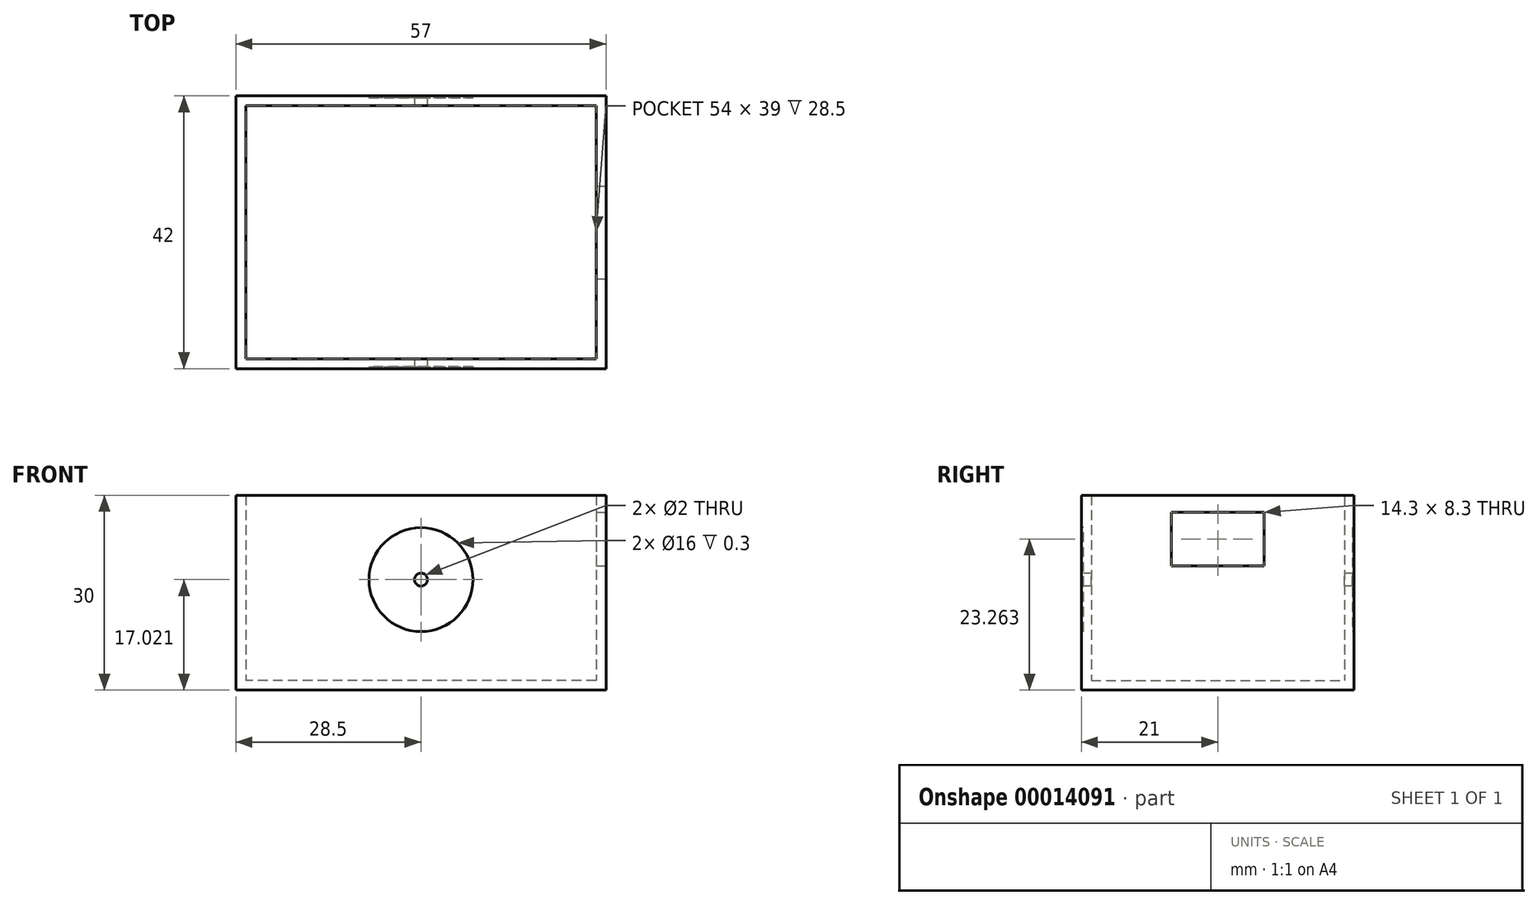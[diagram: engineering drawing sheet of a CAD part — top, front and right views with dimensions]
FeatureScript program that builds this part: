
annotation { "Feature Type Name" : "Feature", "Feature Type Description" : "" }
export const myFeature = defineFeature(function(context is Context, id is Id, definition is map)
    precondition{}
    {
        {
            var Q0;
            Q0=qCreatedBy(makeId("Top.planeOp"),FACE);
            var sketch = newSketch(context, id + "F0", { "sketchPlane" : qUnion([Q0])});
            skLineSegment(sketch, "E0.rect.bottom", {"start": v(28.5, -21) * mm, "end": v(-28.5, -21) * mm});
            skLineSegment(sketch, "E0.rect.top", {"start": v(28.5, 21) * mm, "end": v(-28.5, 21) * mm});
            skLineSegment(sketch, "E0.rect.left", {"start": v(28.5, -21) * mm, "end": v(28.5, 21) * mm});
            skLineSegment(sketch, "E0.rect.right", {"start": v(-28.5, -21) * mm, "end": v(-28.5, 21) * mm});
            skPoint(sketch, "E0.rect.middle", {"position": v(0, 0) * mm});
            skSolve(sketch);
        }
        {
            var Q0;
            Q0=makeQuery(id+"F0.imprint","IMPRINT",FACE,{"disambiguationData":[TD([[makeQuery(id+"F0.imprint","IMPRINT",EDGE,{"derivedFrom":sQuery(id+"F0.wireOp",EDGE,"E0.rect.bottom")}),-1.0]])]});
            extrude(context, id + "F1", {"entities" : qUnion([Q0]), "depth" : 30 * mm});
        }
        {
            var Q0;
            Q0=makeQuery(id+"F1.opExtrude","CAP_FACE",FACE,{"disambiguationData":[OSD([sQuery(id+"F0.wireOp",EDGE,"E0.rect.bottom"),sQuery(id+"F0.wireOp",EDGE,"E0.rect.top"),sQuery(id+"F0.wireOp",EDGE,"E0.rect.left"),sQuery(id+"F0.wireOp",EDGE,"E0.rect.right")])],"isStart":false});
            shell(context, id + "F2", {"entities" : qUnion([Q0]), "thickness" : 1.5 * mm});
        }
        {
            var Q0;
            Q0=makeQuery(id+"F1.opExtrude","SWEPT_FACE",FACE,{"disambiguationData":[OSD([sQuery(id+"F0.wireOp",EDGE,"E0.rect.left")])]});
            var sketch = newSketch(context, id + "F3", { "sketchPlane" : qUnion([Q0])});
            skLineSegment(sketch, "E1.rect.bottom", {"start": v(7.15, 19.11) * mm, "end": v(-7.15, 19.11) * mm});
            skLineSegment(sketch, "E1.rect.top", {"start": v(7.15, 27.41) * mm, "end": v(-7.15, 27.41) * mm});
            skLineSegment(sketch, "E1.rect.left", {"start": v(7.15, 19.11) * mm, "end": v(7.15, 27.41) * mm});
            skLineSegment(sketch, "E1.rect.right", {"start": v(-7.15, 19.11) * mm, "end": v(-7.15, 27.41) * mm});
            skPoint(sketch, "E1.rect.middle", {"position": v(0, 23.26) * mm});
            skSolve(sketch);
        }
        {
            var Q0;
            Q0=makeQuery(id+"F3.imprint","IMPRINT",FACE,{"disambiguationData":[TD([[makeQuery(id+"F3.imprint","IMPRINT",EDGE,{"derivedFrom":sQuery(id+"F3.wireOp",EDGE,"E1.rect.bottom")}),-1.0]])]});
            extrude(context, id + "F4", {"entities" : qUnion([Q0]), "operationType" : NewBodyOperationType.REMOVE, "oppositeDirection" : true, "depth" : 25 * mm});
        }
        {
            var Q0;
            Q0=makeQuery(id+"F1.opExtrude","SWEPT_FACE",FACE,{"disambiguationData":[OSD([sQuery(id+"F0.wireOp",EDGE,"E0.rect.bottom")])]});
            var sketch = newSketch(context, id + "F5", { "sketchPlane" : qUnion([Q0])});
            skCircle(sketch, "E2", {"center": v(0, 17.02) * mm, "radius": 1 * mm});
            skSolve(sketch);
        }
        {
            var Q0;
            Q0=makeQuery(id+"F5.imprint","IMPRINT",FACE,{"disambiguationData":[TD([[makeQuery(id+"F5.imprint","IMPRINT",EDGE,{"derivedFrom":sQuery(id+"F5.wireOp",EDGE,"E2")}),1.0]])]});
            var Q1;
            Q1=sQuery(id+"F5.wireOp",EDGE,"E2");
            extrude(context, id + "F6", {"entities" : qUnion([Q0]), "operationType" : NewBodyOperationType.REMOVE, "surfaceEntities" : qUnion([Q1]), "oppositeDirection" : true, "depth" : 60.38 * mm});
        }
        {
            var Q0;
            Q0=makeQuery(id+"F1.opExtrude","SWEPT_FACE",FACE,{"disambiguationData":[OSD([sQuery(id+"F0.wireOp",EDGE,"E0.rect.bottom")])]});
            var sketch = newSketch(context, id + "F7", { "sketchPlane" : qUnion([Q0])});
            skCircle(sketch, "E3", {"center": v(0, 17.02) * mm, "radius": 8 * mm});
            skSolve(sketch);
        }
        {
            var Q0;
            Q0=makeQuery(id+"F7.imprint","IMPRINT",FACE,{"disambiguationData":[TD([[makeQuery(id+"F7.imprint","IMPRINT",EDGE,{"derivedFrom":sQuery(id+"F7.wireOp",EDGE,"E3")}),1.0]])]});
            extrude(context, id + "F8", {"entities" : qUnion([Q0]), "operationType" : NewBodyOperationType.REMOVE, "oppositeDirection" : true, "depth" : .3 * mm});
        }
        {
            var Q0;
            Q0=makeQuery(id+"F1.opExtrude","SWEPT_FACE",FACE,{"disambiguationData":[OSD([sQuery(id+"F0.wireOp",EDGE,"E0.rect.top")])]});
            var sketch = newSketch(context, id + "F9", { "sketchPlane" : qUnion([Q0])});
            skCircle(sketch, "E4", {"center": v(0, 17.02) * mm, "radius": 8 * mm});
            skSolve(sketch);
        }
        {
            var Q0;
            Q0=makeQuery(id+"F9.imprint","IMPRINT",FACE,{"disambiguationData":[TD([[makeQuery(id+"F9.imprint","IMPRINT",EDGE,{"derivedFrom":sQuery(id+"F9.wireOp",EDGE,"E4")}),1.0]])]});
            extrude(context, id + "F10", {"entities" : qUnion([Q0]), "operationType" : NewBodyOperationType.REMOVE, "oppositeDirection" : true, "depth" : .3 * mm});
        }
    });
